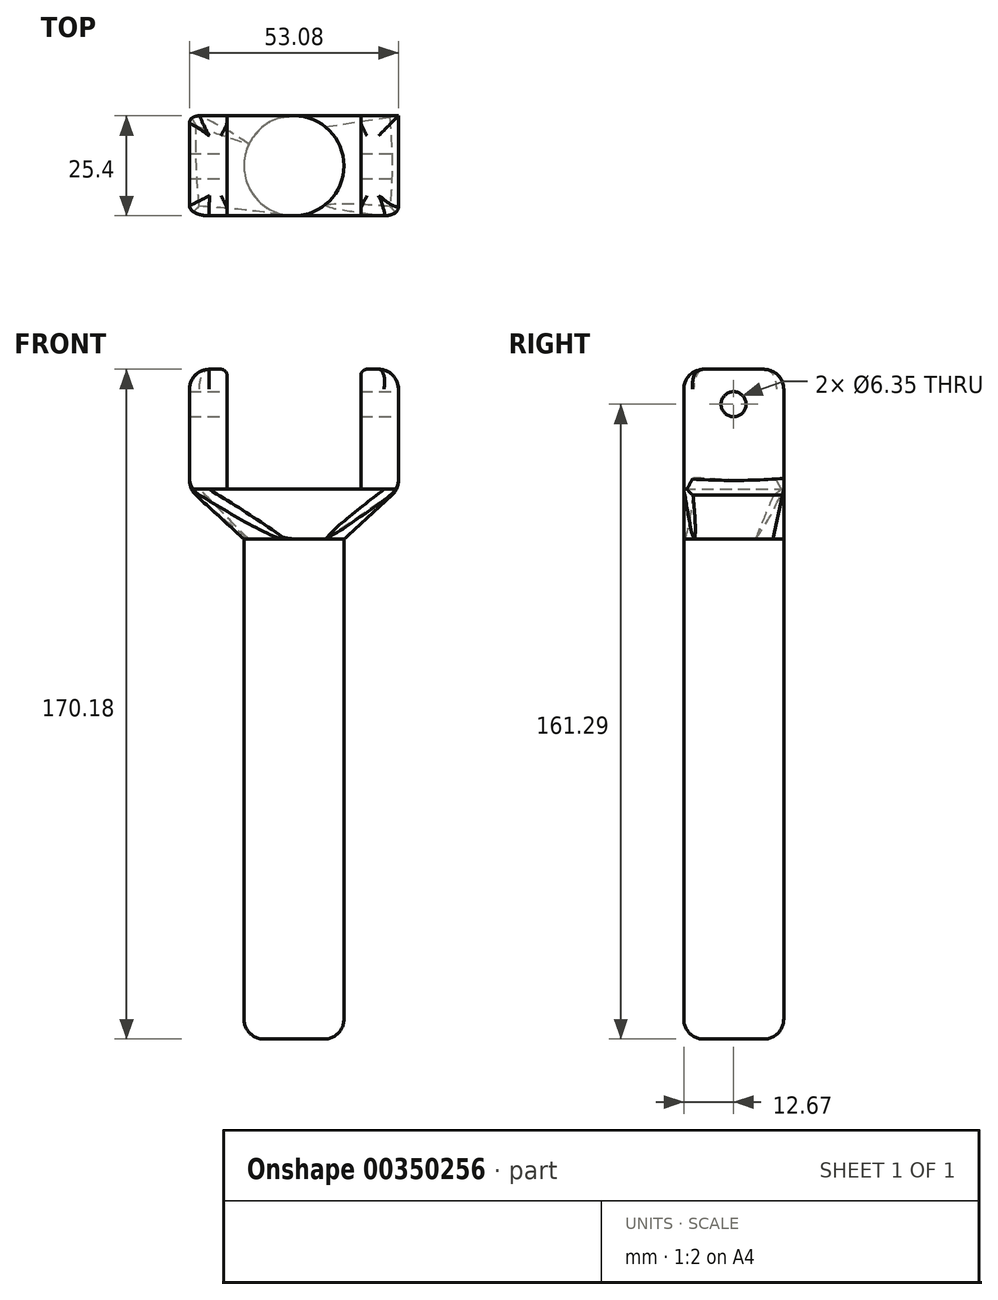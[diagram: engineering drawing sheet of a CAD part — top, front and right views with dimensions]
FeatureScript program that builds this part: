
annotation { "Feature Type Name" : "Feature", "Feature Type Description" : "" }
export const myFeature = defineFeature(function(context is Context, id is Id, definition is map)
    precondition{}
    {
        {
            var Q0;
            Q0=qCreatedBy(makeId("Top.planeOp"),FACE);
            var sketch = newSketch(context, id + "F0", { "sketchPlane" : qUnion([Q0])});
            skCircle(sketch, "E0", {"center": v(0, 0) * mm, "radius": 12.7 * mm});
            skSolve(sketch);
        }
        {
            var Q0;
            Q0=makeQuery(id+"F0.imprint","IMPRINT",FACE,{"disambiguationData":[TD([[makeQuery(id+"F0.imprint","IMPRINT",EDGE,{"derivedFrom":sQuery(id+"F0.wireOp",EDGE,"E0")}),1.0]])]});
            extrude(context, id + "F1", {"entities" : qUnion([Q0]), "oppositeDirection" : true, "depth" : 127 * mm});
        }
        {
            var Q0;
            Q0=makeQuery(id+"F1.opExtrude","CAP_FACE",FACE,{"disambiguationData":[OSD([sQuery(id+"F0.wireOp",EDGE,"E0")])],"isStart":true});
            var sketch = newSketch(context, id + "F2", { "sketchPlane" : qUnion([Q0])});
            skCircle(sketch, "E1", {"center": v(0, 0) * mm, "radius": 12.7 * mm});
            skSolve(sketch);
        }
        {
            var Q0;
            Q0=qCreatedBy(makeId("Top.planeOp"),FACE);
            cPlane(context, id + "F3", {"entities" : qUnion([Q0]), "cplaneType" : CPlaneType.OFFSET, "offset" : 12.7 * mm, "width" : 152.4 * mm, "height" : 152.4 * mm});
        }
        {
            var Q0;
            Q0=qCreatedBy(id+"F3.planeOp",FACE);
            var sketch = newSketch(context, id + "F4", { "sketchPlane" : qUnion([Q0])});
            skLineSegment(sketch, "E2", {"start": v(26.54, 0) * mm, "end": v(26.54, 12.7) * mm});
            skLineSegment(sketch, "E3", {"start": v(-26.54, 0) * mm, "end": v(-26.54, 12.7) * mm});
            skLineSegment(sketch, "E4", {"start": v(26.54, 0) * mm, "end": v(26.54, -12.7) * mm});
            skLineSegment(sketch, "E5", {"start": v(0, 12.7) * mm, "end": v(-26.54, 12.7) * mm});
            skLineSegment(sketch, "E6", {"start": v(0, 12.7) * mm, "end": v(26.54, 12.7) * mm});
            skLineSegment(sketch, "E7", {"start": v(26.54, -12.7) * mm, "end": v(-26.54, -12.7) * mm});
            skLineSegment(sketch, "E8", {"start": v(-26.54, 0) * mm, "end": v(-26.54, -12.7) * mm});
            skSolve(sketch);
        }
        {
            var Q0;
            Q0=makeQuery(id+"F2.imprint","IMPRINT",FACE,{"disambiguationData":[TD([[makeQuery(id+"F2.imprint","IMPRINT",EDGE,{"derivedFrom":sQuery(id+"F2.wireOp",EDGE,"E1")}),1.0]])]});
            var Q1;
            Q1=makeQuery(id+"F4.imprint","IMPRINT",FACE,{"disambiguationData":[TD([[makeQuery(id+"F4.imprint","IMPRINT",EDGE,{"derivedFrom":sQuery(id+"F4.wireOp",EDGE,"E2")}),1.0]])]});
            loft(context, id + "F5", {"sheetProfilesArray" : [{ "sheetProfileEntities" : qUnion([Q0]) }, { "sheetProfileEntities" : qUnion([Q1]) }]});
        }
        {
            var Q0;
            Q0=makeQuery(id+"F5.opLoft","SWEPT_EDGE",EDGE,{"disambiguationData":[OSD([sQuery(id+"F2.wireOp",EDGE,"E1"),sQuery(id+"F4.wireOp",EDGE,"E3"),sQuery(id+"F4.wireOp",EDGE,"E5"),sQuery(id+"F4.wireOp",EDGE,"E6")])]});
            var Q1;
            Q1=makeQuery(id+"F5.opLoft","SWEPT_EDGE",EDGE,{"disambiguationData":[OSD([sQuery(id+"F2.wireOp",EDGE,"E1"),sQuery(id+"F4.wireOp",EDGE,"E2"),sQuery(id+"F4.wireOp",EDGE,"E4"),sQuery(id+"F4.wireOp",EDGE,"E6")])]});
            var Q2;
            Q2=makeQuery(id+"F5.opLoft","SWEPT_EDGE",EDGE,{"disambiguationData":[OSD([sQuery(id+"F2.wireOp",EDGE,"E1"),sQuery(id+"F4.wireOp",EDGE,"E3"),sQuery(id+"F4.wireOp",EDGE,"E7"),sQuery(id+"F4.wireOp",EDGE,"E8")])]});
            var Q3;
            Q3=makeQuery(id+"F5.opLoft","SWEPT_EDGE",EDGE,{"disambiguationData":[OSD([sQuery(id+"F2.wireOp",EDGE,"E1"),sQuery(id+"F4.wireOp",EDGE,"E4"),sQuery(id+"F4.wireOp",EDGE,"E7"),sQuery(id+"F4.wireOp",EDGE,"E8")])]});
            fillet(context, id + "F6", {"entities" : qUnion([Q0, Q1, Q2, Q3]), "radius" : 2.54 * mm, "tangentPropagation" : true, "allowEdgeOverflow" : false});
        }
        {
            var Q0;
            Q0=makeQuery(id+"F5.opLoft","CAP_FACE",FACE,{"disambiguationData":[OSD([makeQuery(id+"F4.imprint","IMPRINT",FACE,{"disambiguationData":[TD([[makeQuery(id+"F4.imprint","IMPRINT",EDGE,{"derivedFrom":sQuery(id+"F4.wireOp",EDGE,"E2")}),1.0]])]})])],"isStart":true});
            var sketch = newSketch(context, id + "F7", { "sketchPlane" : qUnion([Q0])});
            skLineSegment(sketch, "E9", {"start": v(-17.02, -10.18) * mm, "end": v(-17.02, 12.7) * mm});
            skLineSegment(sketch, "E10", {"start": v(-17.02, -10.18) * mm, "end": v(-17.02, -12.7) * mm});
            skLineSegment(sketch, "E11", {"start": v(0, 0) * mm, "end": v(0, 6.7) * mm});
            skLineSegment(sketch, "E12", {"start": v(0, 6.7) * mm, "end": v(0, -9.1) * mm});
            skLineSegment(sketch, "E13.MirrorCS", {"start": v(17.02, -10.18) * mm, "end": v(17.02, 12.7) * mm});
            skLineSegment(sketch, "E14.MirrorCS", {"start": v(17.02, -10.18) * mm, "end": v(17.02, -12.7) * mm});
            skSolve(sketch);
        }
        {
            var Q0;
            Q0 = qSketchRegion(id + "F7", true);
            var Q1;
            {var subQ11=sQuery(id+"F7.wireOp",EDGE,"E9");Q1=makeQuery(id+"F7.imprint","IMPRINT",FACE,{"disambiguationData":[TD([[makeQuery(id+"F7.imprint","IMPRINT",EDGE,{"derivedFrom":subQ11}),1.0]])]});}
            extrude(context, id + "F8", {"entities" : qUnion([Q0, Q1]), "operationType" : NewBodyOperationType.ADD, "depth" : 30.48 * mm});
        }
        {
            var Q0;
            {var subQ11=sQuery(id+"F7.wireOp",EDGE,"E9");Q0=makeQuery(id+"F7.imprint","IMPRINT",FACE,{"disambiguationData":[TD([[makeQuery(id+"F7.imprint","IMPRINT",EDGE,{"derivedFrom":subQ11}),1.0]])]});}
            var Q1;
            {var subQ10=sQuery(id+"F7.wireOp",EDGE,"E13.MirrorCS");Q1=makeQuery(id+"F7.imprint","IMPRINT",FACE,{"disambiguationData":[TD([[makeQuery(id+"F7.imprint","IMPRINT",EDGE,{"derivedFrom":subQ10}),-1.0]])]});}
            extrude(context, id + "F9", {"entities" : qUnion([Q0, Q1]), "operationType" : NewBodyOperationType.ADD, "depth" : 30.48 * mm});
        }
        {
            var Q0;
            Q0=makeQuery(id+"F9.opExtrude","SWEPT_FACE",FACE,{"disambiguationData":[OSD([sQuery(id+"F4.wireOp",EDGE,"E2"),sQuery(id+"F4.wireOp",EDGE,"E4"),sQuery(id+"F4.wireOp",EDGE,"E7")])]});
            var sketch = newSketch(context, id + "F10", { "sketchPlane" : qUnion([Q0])});
            skCircle(sketch, "E15", {"center": v(-0.03, 34.3) * mm, "radius": 3.18 * mm});
            skSolve(sketch);
        }
        {
            var Q0;
            Q0=makeQuery(id+"F10.imprint","IMPRINT",FACE,{"disambiguationData":[TD([[makeQuery(id+"F10.imprint","IMPRINT",EDGE,{"derivedFrom":sQuery(id+"F10.wireOp",EDGE,"E15")}),1.0]])]});
            extrude(context, id + "F11", {"entities" : qUnion([Q0]), "operationType" : NewBodyOperationType.REMOVE, "oppositeDirection" : true, "depth" : 76.2 * mm});
        }
        {
            var Q0;
            Q0=makeQuery(id+"F8.opExtrude","CAP_EDGE",EDGE,{"disambiguationData":[OSD([sQuery(id+"F7.wireOp",EDGE,"E9"),sQuery(id+"F7.wireOp",EDGE,"E10")])],"isStart":true});
            var Q1;
            Q1=makeQuery(id+"F8.opExtrude","CAP_EDGE",EDGE,{"disambiguationData":[OSD([sQuery(id+"F7.wireOp",EDGE,"E9"),sQuery(id+"F7.wireOp",EDGE,"E10")])],"isStart":false});
            var Q2;
            Q2=makeQuery(id+"F9.opExtrude","CAP_EDGE",EDGE,{"disambiguationData":[OSD([sQuery(id+"F7.wireOp",EDGE,"E13.MirrorCS"),sQuery(id+"F7.wireOp",EDGE,"E14.MirrorCS")])],"isStart":true});
            var Q3;
            Q3=makeQuery(id+"F9.opExtrude","CAP_EDGE",EDGE,{"disambiguationData":[OSD([sQuery(id+"F7.wireOp",EDGE,"E13.MirrorCS"),sQuery(id+"F7.wireOp",EDGE,"E14.MirrorCS")])],"isStart":false});
            fillet(context, id + "F12", {"entities" : qUnion([Q0, Q1, Q2, Q3]), "radius" : 1.52 * mm, "tangentPropagation" : true, "allowEdgeOverflow" : false});
        }
        {
            var Q0;
            {var subQ0=sQuery(id+"F4.wireOp",EDGE,"E8");var subQ1=sQuery(id+"F4.wireOp",EDGE,"E7");var subQ2=sQuery(id+"F4.wireOp",EDGE,"E4");var subQ3=makeQuery(id+"F5.opLoft","MID_CAP_EDGE",EDGE,{"disambiguationData":[OSD([subQ2,subQ1,subQ0])],"capPos":1.0});Q0=makeQuery(id+"F9.opExtrude","CAP_EDGE",EDGE,{"disambiguationData":[OSD([subQ2,subQ1,subQ0]),TDD([makeQuery(id+"F7.imprint","IMPRINT",EDGE,{"disambiguationData":[TD([[makeQuery(id+"F7.imprint","INTERSECT",VERTEX,{"derivedFrom":[subQ3,sQuery(id+"F7.wireOp",EDGE,"E14.MirrorCS")]}),-1.0]])],"derivedFrom":subQ3})])],"isStart":false});}
            var Q1;
            Q1=makeQuery(id+"F8.opExtrude","CAP_EDGE",EDGE,{"disambiguationData":[OSD([sQuery(id+"F4.wireOp",EDGE,"E4"),sQuery(id+"F4.wireOp",EDGE,"E7"),sQuery(id+"F4.wireOp",EDGE,"E8")])],"isStart":false});
            var Q2;
            Q2=makeQuery(id+"F8.opExtrude","CAP_EDGE",EDGE,{"disambiguationData":[OSD([sQuery(id+"F4.wireOp",EDGE,"E2"),sQuery(id+"F4.wireOp",EDGE,"E5"),sQuery(id+"F4.wireOp",EDGE,"E6")])],"isStart":false});
            var Q3;
            {var subQ0=sQuery(id+"F4.wireOp",EDGE,"E5");var subQ2=sQuery(id+"F4.wireOp",EDGE,"E2");var subQ3=sQuery(id+"F4.wireOp",EDGE,"E6");var subQ4=makeQuery(id+"F5.opLoft","MID_CAP_EDGE",EDGE,{"disambiguationData":[OSD([subQ2,subQ0,subQ3])],"capPos":1.0});Q3=makeQuery(id+"F9.opExtrude","CAP_EDGE",EDGE,{"disambiguationData":[OSD([subQ2,subQ0,subQ3]),TDD([makeQuery(id+"F7.imprint","IMPRINT",EDGE,{"disambiguationData":[TD([[makeQuery(id+"F7.imprint","INTERSECT",VERTEX,{"derivedFrom":[subQ4,sQuery(id+"F7.wireOp",EDGE,"E13.MirrorCS")]}),1.0]])],"derivedFrom":subQ4})])],"isStart":false});}
            var Q4;
            Q4=makeQuery(id+"F9.opExtrude","CAP_EDGE",EDGE,{"disambiguationData":[OSD([sQuery(id+"F4.wireOp",EDGE,"E2"),sQuery(id+"F4.wireOp",EDGE,"E4"),sQuery(id+"F4.wireOp",EDGE,"E7")])],"isStart":false});
            var Q5;
            Q5=makeQuery(id+"F8.opExtrude","CAP_EDGE",EDGE,{"disambiguationData":[OSD([sQuery(id+"F4.wireOp",EDGE,"E3"),sQuery(id+"F4.wireOp",EDGE,"E5"),sQuery(id+"F4.wireOp",EDGE,"E8")])],"isStart":false});
            var Q6;
            {var subQ0=sQuery(id+"F4.wireOp",EDGE,"E7");var subQ1=sQuery(id+"F4.wireOp",EDGE,"E4");var subQ2=sQuery(id+"F4.wireOp",EDGE,"E2");Q6=makeQuery(id+"F9.boolean.opBoolean","MERGE",EDGE,{"derivedFrom":[makeQuery(id+"F5.opLoft","MID_CAP_EDGE",EDGE,{"disambiguationData":[OSD([subQ2,subQ1,subQ0])],"capPos":1.0}),makeQuery(id+"F9.opExtrude","CAP_EDGE",EDGE,{"disambiguationData":[OSD([subQ2,subQ1,subQ0])],"isStart":true})]});}
            var Q7;
            {var subQ0=sQuery(id+"F4.wireOp",EDGE,"E8");var subQ1=sQuery(id+"F4.wireOp",EDGE,"E5");var subQ2=sQuery(id+"F4.wireOp",EDGE,"E3");Q7=makeQuery(id+"F8.boolean.opBoolean","MERGE",EDGE,{"derivedFrom":[makeQuery(id+"F5.opLoft","MID_CAP_EDGE",EDGE,{"disambiguationData":[OSD([subQ2,subQ1,subQ0])],"capPos":1.0}),makeQuery(id+"F8.opExtrude","CAP_EDGE",EDGE,{"disambiguationData":[OSD([subQ2,subQ1,subQ0])],"isStart":true})]});}
            fillet(context, id + "F13", {"entities" : qUnion([Q0, Q1, Q2, Q3, Q4, Q5, Q6, Q7]), "radius" : 5.08 * mm, "allowEdgeOverflow" : false});
        }
        {
            var Q0;
            Q0=makeQuery(id+"F1.opExtrude","CAP_EDGE",EDGE,{"disambiguationData":[OSD([sQuery(id+"F0.wireOp",EDGE,"E0")])],"isStart":false});
            fillet(context, id + "F14", {"entities" : qUnion([Q0]), "radius" : 5.08 * mm, "tangentPropagation" : true, "allowEdgeOverflow" : false});
        }
    });
